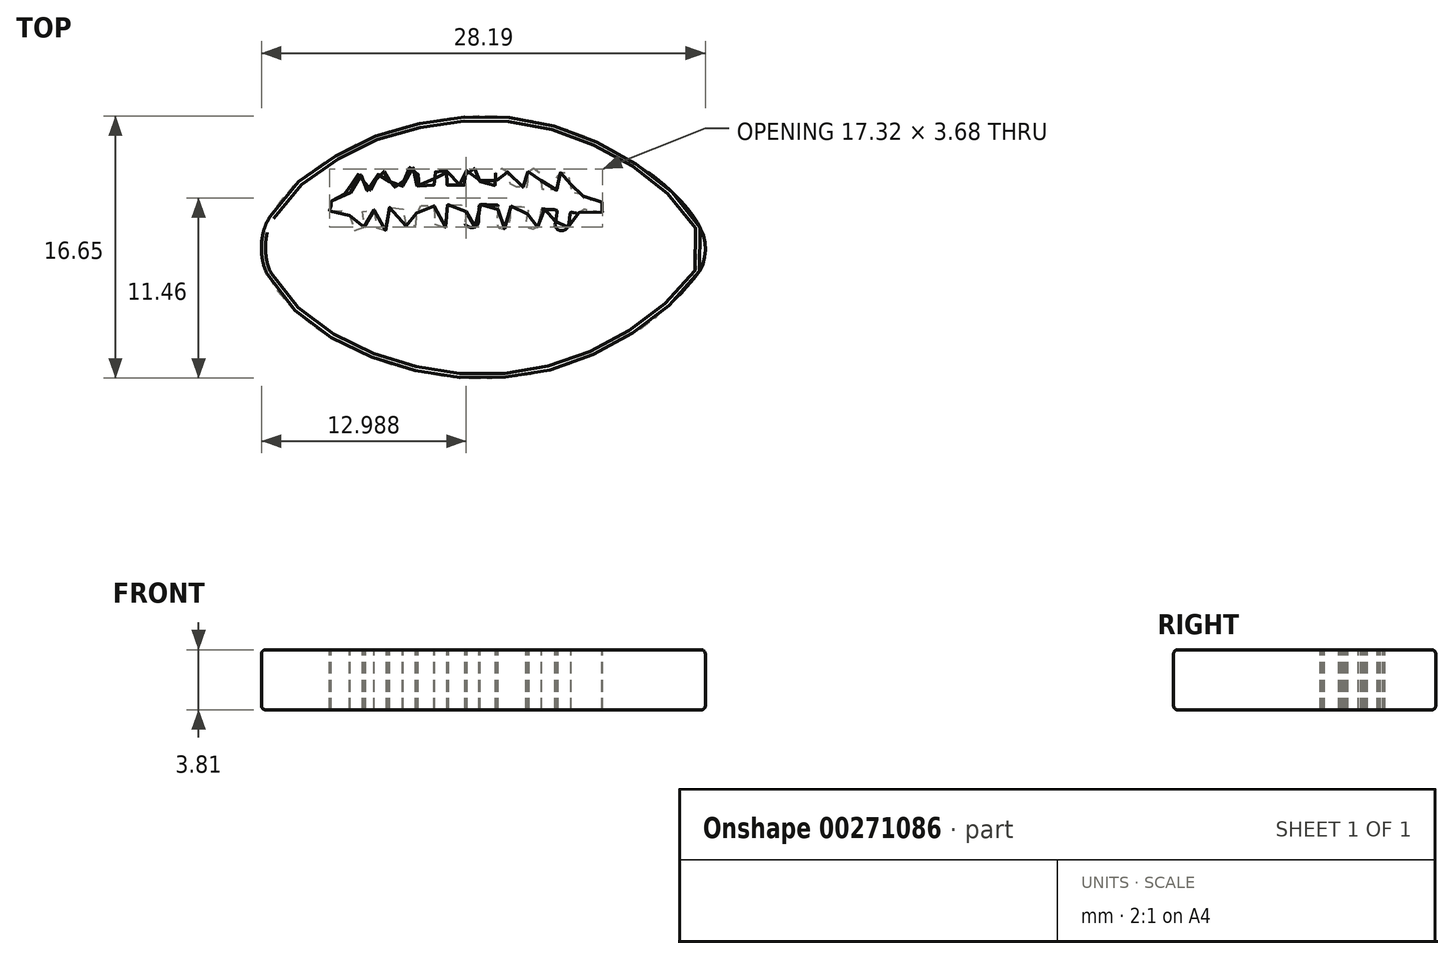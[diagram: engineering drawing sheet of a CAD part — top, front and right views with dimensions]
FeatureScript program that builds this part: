
annotation { "Feature Type Name" : "Feature", "Feature Type Description" : "" }
export const myFeature = defineFeature(function(context is Context, id is Id, definition is map)
    precondition{}
    {
        {
            var Q0;
            Q0=qCreatedBy(makeId("Top.planeOp"),FACE);
            var sketch = newSketch(context, id + "F0", { "sketchPlane" : qUnion([Q0])});
            skPoint(sketch, "E0.middle", {"position": v(0, 0) * mm});
            skFitSpline(sketch, "E1", {"points": [v(13.84, -7.05) * mm, v(13.82, -6.2) * mm, v(13.09, -4.68) * mm, v(11.7, -3.12) * mm, v(9.63, -1.48) * mm, v(6.3, 0.3) * mm, v(3.7, 1.17) * mm, v(0.26, 1.65) * mm, v(-2.3, 1.5) * mm, v(-4.49, 1.14) * mm, v(-6.86, 0.47) * mm, v(-9, -0.52) * mm, v(-11.7, -2.3) * mm, v(-13.11, -3.7) * mm, v(-13.78, -4.7) * mm, v(-14.2, -5.68) * mm, v(-14.3, -7.18) * mm, v(-13.94, -8.42) * mm, v(-12.7, -10.18) * mm, v(-11.83, -10.98) * mm, v(-10.38, -12.1) * mm, v(-9.15, -12.8) * mm, v(-7.28, -13.67) * mm, v(-4.61, -14.5) * mm, v(-1.94, -14.93) * mm, v(0.3, -14.98) * mm, v(3.1, -14.66) * mm, v(5.1, -14.13) * mm, v(6.84, -13.43) * mm, v(9.64, -11.88) * mm, v(11.3, -10.59) * mm, v(12.98, -8.86) * mm, v(13.7, -7.76) * mm, v(13.84, -7.05) * mm]});
            skArc(sketch, "E2", {"start": v(-11.9, -3.32) * mm, "mid": v(-12, -3.9) * mm, "end": v(-12.07, -4.47) * mm});
            skArc(sketch, "E3", {"start": v(-9.3, -1.43) * mm, "mid": v(-9.63, -2.58) * mm, "end": v(-9.87, -3.74) * mm});
            skArc(sketch, "E4", {"start": v(9.72, -11.06) * mm, "mid": v(9.89, -8.05) * mm, "end": v(9.87, -5.03) * mm});
            skArc(sketch, "E5", {"start": v(6.96, -12.67) * mm, "mid": v(7.34, -8.57) * mm, "end": v(7.33, -4.45) * mm});
            skArc(sketch, "E6", {"start": v(13.23, -6.62) * mm, "mid": v(11.6, -5.7) * mm, "end": v(9.87, -5.03) * mm});
            skArc(sketch, "E7", {"start": v(12.96, -5.7) * mm, "mid": v(11.43, -4.97) * mm, "end": v(9.85, -4.37) * mm});
            skArc(sketch, "E8", {"start": v(-12.13, -5.1) * mm, "mid": v(-12.95, -5.5) * mm, "end": v(-13.64, -6.09) * mm});
            skArc(sketch, "E9", {"start": v(-12.07, -4.47) * mm, "mid": v(-12.65, -4.7) * mm, "end": v(-13.2, -4.99) * mm});
            skFitSpline(sketch, "E10", {"points": [v(-9.97, -4.38) * mm, v(-9.32, -4.28) * mm, v(-9.2, -4.31) * mm, v(-9.03, -4.45) * mm, v(-8.74, -4.5) * mm, v(-8.71, -4.66) * mm, v(-8.6, -5.39) * mm, v(-8.29, -5.65) * mm, v(-7.97, -5.6) * mm, v(-7.81, -5.38) * mm, v(-7.79, -5.18) * mm, v(-7.89, -4.38) * mm, v(-7.78, -4.35) * mm, v(-7.2, -4.28) * mm, v(-7.17, -4.4) * mm, v(-7.05, -5.35) * mm, v(-6.93, -5.58) * mm, v(-6.62, -5.67) * mm, v(-6.35, -5.53) * mm, v(-6.23, -5.3) * mm, v(-6.24, -5.08) * mm, v(-6.36, -4.18) * mm, v(-6.23, -4.14) * mm, v(-5.37, -4.08) * mm, v(-5.35, -4.27) * mm, v(-5.23, -5.12) * mm, v(-5.06, -5.36) * mm, v(-4.74, -5.4) * mm, v(-4.52, -5.27) * mm, v(-4.4, -5.04) * mm, v(-4.43, -4.76) * mm, v(-4.53, -4.03) * mm, v(-4.4, -4.02) * mm, v(-3.8, -3.98) * mm, v(-3.4, -3.97) * mm, v(-3.36, -4.2) * mm, v(-3.32, -5.2) * mm, v(-3.11, -5.42) * mm, v(-2.74, -5.44) * mm, v(-2.52, -5.24) * mm, v(-2.5, -5.07) * mm, v(-2.51, -4.72) * mm, v(-2.53, -4.16) * mm, v(-2.5, -3.98) * mm, v(-2.2, -3.94) * mm, v(-1.66, -3.96) * mm, v(-1.32, -3.96) * mm, v(-1.32, -4.24) * mm, v(-1.36, -4.72) * mm, v(-1.41, -5.06) * mm, v(-1.3, -5.3) * mm, v(-0.98, -5.42) * mm, v(-0.7, -5.34) * mm, v(-0.57, -5.12) * mm, v(-0.53, -4.72) * mm, v(-0.48, -4.3) * mm, v(-0.46, -3.98) * mm, v(-0.17, -3.96) * mm, v(0.14, -3.98) * mm, v(0.48, -3.98) * mm, v(0.7, -4) * mm, v(0.7, -4.23) * mm, v(0.63, -4.86) * mm, v(0.6, -5.13) * mm, v(0.72, -5.4) * mm, v(0.97, -5.5) * mm, v(1.2, -5.46) * mm, v(1.37, -5.3) * mm, v(1.46, -4.91) * mm, v(1.5, -4.54) * mm, v(1.55, -4.05) * mm, v(1.7, -4.05) * mm, v(2.04, -4.1) * mm, v(2.63, -4.12) * mm, v(2.63, -4.26) * mm, v(2.52, -4.76) * mm, v(2.48, -5.16) * mm, v(2.64, -5.44) * mm, v(2.97, -5.5) * mm, v(3.22, -5.37) * mm, v(3.32, -5.08) * mm, v(3.38, -4.74) * mm, v(3.43, -4.48) * mm, v(3.45, -4.24) * mm, v(3.71, -4.25) * mm, v(4.06, -4.28) * mm, v(4.45, -4.34) * mm, v(4.45, -4.49) * mm, v(4.39, -4.86) * mm, v(4.33, -5.22) * mm, v(4.37, -5.4) * mm, v(4.55, -5.57) * mm, v(4.83, -5.6) * mm, v(5.05, -5.5) * mm, v(5.16, -5.33) * mm, v(5.21, -5.07) * mm, v(5.3, -4.45) * mm, v(5.38, -4.45) * mm, v(5.7, -4.49) * mm, v(5.95, -4.41) * mm, v(6.12, -4.27) * mm, v(6.37, -4.28) * mm, v(6.9, -4.38) * mm, v(7.33, -4.45) * mm, v(7.32, -4.4) * mm, v(7.31, -4.18) * mm, v(7.3, -3.84) * mm, v(7.29, -3.8) * mm, v(7, -3.76) * mm, v(6.52, -3.68) * mm, v(6.23, -3.65) * mm, v(6.16, -3.52) * mm, v(6.05, -3.37) * mm, v(5.83, -3.24) * mm, v(5.34, -3.19) * mm, v(5.33, -3.1) * mm, v(5.31, -2.75) * mm, v(5.26, -2.45) * mm, v(5.22, -2.22) * mm, v(5.1, -2.01) * mm, v(4.92, -1.94) * mm, v(4.7, -1.92) * mm, v(4.5, -2.05) * mm, v(4.37, -2.26) * mm, v(4.42, -2.57) * mm, v(4.5, -3.05) * mm, v(4.39, -3.04) * mm, v(3.97, -3) * mm, v(3.51, -2.98) * mm, v(3.48, -2.81) * mm, v(3.43, -2.4) * mm, v(3.35, -1.99) * mm, v(3.19, -1.78) * mm, v(2.93, -1.69) * mm, v(2.66, -1.8) * mm, v(2.54, -2.06) * mm, v(2.54, -2.33) * mm, v(2.65, -2.86) * mm, v(2.5, -2.88) * mm, v(2.08, -2.85) * mm, v(1.52, -2.82) * mm, v(1.5, -2.6) * mm, v(1.34, -1.93) * mm, v(1.15, -1.75) * mm, v(0.86, -1.68) * mm, v(0.6, -1.86) * mm, v(0.54, -2.2) * mm, v(0.67, -2.74) * mm, v(0.47, -2.74) * mm, v(-0.4, -2.7) * mm, v(-0.45, -2.53) * mm, v(-0.5, -1.96) * mm, v(-0.68, -1.72) * mm, v(-0.95, -1.63) * mm, v(-1.23, -1.72) * mm, v(-1.37, -1.97) * mm, v(-1.31, -2.26) * mm, v(-1.29, -2.7) * mm, v(-1.43, -2.72) * mm, v(-1.95, -2.7) * mm, v(-2.53, -2.72) * mm, v(-2.5, -2.54) * mm, v(-2.45, -2.03) * mm, v(-2.63, -1.75) * mm, v(-2.9, -1.66) * mm, v(-3.24, -1.8) * mm, v(-3.3, -2.07) * mm, v(-3.34, -2.43) * mm, v(-3.35, -2.7) * mm, v(-3.56, -2.7) * mm, v(-3.92, -2.72) * mm, v(-4.48, -2.75) * mm, v(-4.47, -2.57) * mm, v(-4.37, -2.1) * mm, v(-4.43, -1.8) * mm, v(-4.65, -1.63) * mm, v(-4.94, -1.6) * mm, v(-5.15, -1.8) * mm, v(-5.26, -2.17) * mm, v(-5.36, -2.8) * mm, v(-5.5, -2.85) * mm, v(-5.8, -2.85) * mm, v(-6.26, -2.9) * mm, v(-6.26, -2.75) * mm, v(-6.18, -2.36) * mm, v(-6.24, -2.09) * mm, v(-6.35, -1.93) * mm, v(-6.66, -1.86) * mm, v(-6.9, -2) * mm, v(-7, -2.23) * mm, v(-7.11, -2.57) * mm, v(-7.16, -2.98) * mm, v(-7.31, -3.02) * mm, v(-7.82, -3.1) * mm, v(-7.8, -2.9) * mm, v(-7.72, -2.54) * mm, v(-7.82, -2.23) * mm, v(-8.05, -2.06) * mm, v(-8.39, -2.12) * mm, v(-8.56, -2.37) * mm, v(-8.63, -2.7) * mm, v(-8.7, -3.25) * mm, v(-8.85, -3.25) * mm, v(-9.14, -3.37) * mm, v(-9.38, -3.66) * mm, v(-9.87, -3.74) * mm, v(-9.9, -3.87) * mm, v(-9.93, -4.14) * mm, v(-9.97, -4.38) * mm]});
            skFitSpline(sketch, "E11.0", {"points": [v(13.2, -7.07) * mm, v(13.21, -7) * mm, v(13.22, -6.92) * mm, v(13.22, -6.83) * mm, v(13.23, -6.71) * mm, v(13.23, -6.6) * mm, v(13.23, -6.53) * mm, v(13.22, -6.46) * mm, v(13.21, -6.41) * mm, v(13.2, -6.36) * mm, v(13.2, -6.3) * mm, v(13.16, -6.19) * mm, v(13.1, -6.02) * mm, v(13, -5.78) * mm, v(12.83, -5.45) * mm, v(12.57, -5.05) * mm, v(12.29, -4.66) * mm, v(11.97, -4.29) * mm, v(11.68, -3.98) * mm, v(11.43, -3.74) * mm, v(11.27, -3.59) * mm, v(11.14, -3.46) * mm, v(11, -3.35) * mm, v(10.77, -3.14) * mm, v(10.43, -2.84) * mm, v(9.97, -2.48) * mm, v(9.47, -2.13) * mm, v(8.91, -1.77) * mm, v(8.1, -1.29) * mm, v(7.24, -0.83) * mm, v(6.4, -0.43) * mm, v(5.61, -0.08) * mm, v(4.9, 0.18) * mm, v(4.18, 0.4) * mm, v(3.42, 0.58) * mm, v(2.54, 0.76) * mm, v(1.63, 0.9) * mm, v(1.07, 0.96) * mm, v(0.68, 1) * mm, v(0.47, 1) * mm, v(0.26, 1.02) * mm, v(0, 1.03) * mm, v(-0.3, 1.03) * mm, v(-0.6, 1.02) * mm, v(-0.97, 1) * mm, v(-1.43, 0.97) * mm, v(-1.98, 0.9) * mm, v(-2.52, 0.84) * mm, v(-3.04, 0.76) * mm, v(-3.48, 0.7) * mm, v(-3.83, 0.63) * mm, v(-4.18, 0.56) * mm, v(-4.63, 0.46) * mm, v(-5.18, 0.33) * mm, v(-5.73, 0.17) * mm, v(-6.27, 0) * mm, v(-6.78, -0.18) * mm, v(-7.26, -0.37) * mm, v(-7.74, -0.58) * mm, v(-8.14, -0.78) * mm, v(-8.48, -0.96) * mm, v(-8.74, -1.1) * mm, v(-9.01, -1.26) * mm, v(-9.38, -1.48) * mm, v(-9.86, -1.77) * mm, v(-10.33, -2.08) * mm, v(-10.68, -2.32) * mm, v(-10.94, -2.51) * mm, v(-11.18, -2.7) * mm, v(-11.41, -2.88) * mm, v(-11.62, -3.06) * mm, v(-11.88, -3.3) * mm, v(-12.17, -3.58) * mm, v(-12.46, -3.9) * mm, v(-12.67, -4.18) * mm, v(-12.82, -4.38) * mm, v(-12.97, -4.6) * mm, v(-13.08, -4.77) * mm, v(-13.16, -4.92) * mm, v(-13.2, -4.97) * mm, v(-13.23, -5.02) * mm, v(-13.26, -5.08) * mm, v(-13.3, -5.16) * mm, v(-13.35, -5.23) * mm, v(-13.4, -5.33) * mm, v(-13.44, -5.42) * mm, v(-13.48, -5.51) * mm, v(-13.5, -5.58) * mm, v(-13.54, -5.65) * mm, v(-13.56, -5.72) * mm, v(-13.57, -5.76) * mm, v(-13.58, -5.8) * mm, v(-13.6, -5.84) * mm, v(-13.6, -5.9) * mm, v(-13.62, -5.96) * mm, v(-13.63, -6.05) * mm, v(-13.65, -6.15) * mm, v(-13.66, -6.28) * mm, v(-13.68, -6.45) * mm, v(-13.68, -6.66) * mm, v(-13.68, -6.86) * mm, v(-13.67, -7.03) * mm, v(-13.66, -7.16) * mm, v(-13.65, -7.28) * mm, v(-13.64, -7.38) * mm, v(-13.62, -7.49) * mm, v(-13.6, -7.56) * mm, v(-13.58, -7.64) * mm, v(-13.56, -7.71) * mm, v(-13.53, -7.79) * mm, v(-13.5, -7.87) * mm, v(-13.47, -7.94) * mm, v(-13.4, -8.07) * mm, v(-13.34, -8.2) * mm, v(-13.27, -8.32) * mm, v(-13.2, -8.43) * mm, v(-13.14, -8.54) * mm, v(-13.04, -8.69) * mm, v(-12.95, -8.83) * mm, v(-12.84, -8.98) * mm, v(-12.76, -9.1) * mm, v(-12.68, -9.2) * mm, v(-12.6, -9.3) * mm, v(-12.52, -9.4) * mm, v(-12.44, -9.5) * mm, v(-12.37, -9.6) * mm, v(-12.3, -9.68) * mm, v(-12.22, -9.77) * mm, v(-12.15, -9.84) * mm, v(-12.09, -9.9) * mm, v(-12, -10) * mm, v(-11.92, -10.07) * mm, v(-11.84, -10.15) * mm, v(-11.77, -10.2) * mm, v(-11.7, -10.26) * mm, v(-11.61, -10.34) * mm, v(-11.49, -10.44) * mm, v(-11.25, -10.63) * mm, v(-10.94, -10.89) * mm, v(-10.54, -11.2) * mm, v(-10.24, -11.42) * mm, v(-10.06, -11.55) * mm, v(-9.93, -11.63) * mm, v(-9.79, -11.72) * mm, v(-9.62, -11.83) * mm, v(-9.44, -11.92) * mm, v(-9.3, -12) * mm, v(-9.18, -12.07) * mm, v(-9.05, -12.13) * mm, v(-8.88, -12.21) * mm, v(-8.6, -12.36) * mm, v(-8.24, -12.54) * mm, v(-7.77, -12.77) * mm, v(-7.36, -12.95) * mm, v(-7.05, -13.08) * mm, v(-6.88, -13.15) * mm, v(-6.61, -13.25) * mm, v(-6.02, -13.46) * mm, v(-5.05, -13.75) * mm, v(-4.05, -13.98) * mm, v(-3.26, -14.12) * mm, v(-2.77, -14.2) * mm, v(-2.4, -14.24) * mm, v(-2.02, -14.28) * mm, v(-1.57, -14.32) * mm, v(-1.05, -14.35) * mm, v(-0.53, -14.37) * mm, v(0, -14.36) * mm, v(0.57, -14.33) * mm, v(1.17, -14.29) * mm, v(1.79, -14.22) * mm, v(2.4, -14.14) * mm, v(3.17, -14) * mm, v(3.86, -13.84) * mm, v(4.5, -13.66) * mm, v(4.87, -13.54) * mm, v(5.16, -13.44) * mm, v(5.44, -13.34) * mm, v(5.8, -13.2) * mm, v(6.25, -13) * mm, v(6.76, -12.77) * mm, v(7.33, -12.48) * mm, v(7.83, -12.22) * mm, v(8.22, -12) * mm, v(8.62, -11.77) * mm, v(8.98, -11.55) * mm, v(9.32, -11.34) * mm, v(9.55, -11.18) * mm, v(9.76, -11.03) * mm, v(10.03, -10.84) * mm, v(10.28, -10.64) * mm, v(10.53, -10.43) * mm, v(10.72, -10.26) * mm, v(10.9, -10.08) * mm, v(11.18, -9.83) * mm, v(11.52, -9.5) * mm, v(11.93, -9.08) * mm, v(12.24, -8.74) * mm, v(12.47, -8.48) * mm, v(12.62, -8.3) * mm, v(12.76, -8.12) * mm, v(12.85, -8) * mm, v(12.92, -7.9) * mm, v(12.98, -7.8) * mm, v(13.03, -7.7) * mm, v(13.07, -7.63) * mm, v(13.1, -7.58) * mm, v(13.1, -7.55) * mm, v(13.12, -7.51) * mm, v(13.13, -7.47) * mm, v(13.15, -7.42) * mm, v(13.16, -7.37) * mm, v(13.17, -7.32) * mm, v(13.18, -7.24) * mm, v(13.2, -7.16) * mm, v(13.2, -7.07) * mm, v(13.21, -7) * mm, v(13.22, -6.92) * mm]});
            skArc(sketch, "E12.trimOffspring", {"start": v(-12.13, -5.1) * mm, "mid": v(-12.2, -7.55) * mm, "end": v(-12, -10) * mm});
            skArc(sketch, "E13.trimOffspring", {"start": v(-9.97, -4.38) * mm, "mid": v(-10.1, -8.19) * mm, "end": v(-9.42, -11.93) * mm});
            skFitSpline(sketch, "E14.trimOffspring", {"points": [v(13.2, -7.07) * mm, v(13.21, -7) * mm, v(13.22, -6.92) * mm, v(13.22, -6.83) * mm, v(13.23, -6.71) * mm, v(13.23, -6.6) * mm, v(13.23, -6.53) * mm, v(13.22, -6.46) * mm, v(13.21, -6.41) * mm, v(13.2, -6.36) * mm, v(13.2, -6.3) * mm, v(13.16, -6.19) * mm, v(13.1, -6.02) * mm, v(13, -5.78) * mm, v(12.83, -5.45) * mm, v(12.57, -5.05) * mm, v(12.29, -4.66) * mm, v(11.97, -4.29) * mm, v(11.68, -3.98) * mm, v(11.43, -3.74) * mm, v(11.27, -3.59) * mm, v(11.14, -3.46) * mm, v(11, -3.35) * mm, v(10.77, -3.14) * mm, v(10.43, -2.84) * mm, v(9.97, -2.48) * mm, v(9.47, -2.13) * mm, v(8.91, -1.77) * mm, v(8.1, -1.29) * mm, v(7.24, -0.83) * mm, v(6.4, -0.43) * mm, v(5.61, -0.08) * mm, v(4.9, 0.18) * mm, v(4.18, 0.4) * mm, v(3.42, 0.58) * mm, v(2.54, 0.76) * mm, v(1.63, 0.9) * mm, v(1.07, 0.96) * mm, v(0.68, 1) * mm, v(0.47, 1) * mm, v(0.26, 1.02) * mm, v(0, 1.03) * mm, v(-0.3, 1.03) * mm, v(-0.6, 1.02) * mm, v(-0.97, 1) * mm, v(-1.43, 0.97) * mm, v(-1.98, 0.9) * mm, v(-2.52, 0.84) * mm, v(-3.04, 0.76) * mm, v(-3.48, 0.7) * mm, v(-3.83, 0.63) * mm, v(-4.18, 0.56) * mm, v(-4.63, 0.46) * mm, v(-5.18, 0.33) * mm, v(-5.73, 0.17) * mm, v(-6.27, 0) * mm, v(-6.78, -0.18) * mm, v(-7.26, -0.37) * mm, v(-7.74, -0.58) * mm, v(-8.14, -0.78) * mm, v(-8.48, -0.96) * mm, v(-8.74, -1.1) * mm, v(-9.01, -1.26) * mm, v(-9.38, -1.48) * mm, v(-9.86, -1.77) * mm, v(-10.33, -2.08) * mm, v(-10.68, -2.32) * mm, v(-10.94, -2.51) * mm, v(-11.18, -2.7) * mm, v(-11.41, -2.88) * mm, v(-11.62, -3.06) * mm, v(-11.88, -3.3) * mm, v(-12.17, -3.58) * mm, v(-12.46, -3.9) * mm, v(-12.67, -4.18) * mm, v(-12.82, -4.38) * mm, v(-12.97, -4.6) * mm, v(-13.08, -4.77) * mm, v(-13.16, -4.92) * mm, v(-13.2, -4.97) * mm, v(-13.23, -5.02) * mm, v(-13.26, -5.08) * mm, v(-13.3, -5.16) * mm, v(-13.35, -5.23) * mm, v(-13.4, -5.33) * mm, v(-13.44, -5.42) * mm, v(-13.48, -5.51) * mm, v(-13.5, -5.58) * mm, v(-13.54, -5.65) * mm, v(-13.56, -5.72) * mm, v(-13.57, -5.76) * mm, v(-13.58, -5.8) * mm, v(-13.6, -5.84) * mm, v(-13.6, -5.9) * mm, v(-13.62, -5.96) * mm, v(-13.63, -6.05) * mm, v(-13.65, -6.15) * mm, v(-13.66, -6.28) * mm, v(-13.68, -6.45) * mm, v(-13.68, -6.66) * mm, v(-13.68, -6.86) * mm, v(-13.67, -7.03) * mm, v(-13.66, -7.16) * mm, v(-13.65, -7.28) * mm, v(-13.64, -7.38) * mm, v(-13.62, -7.49) * mm, v(-13.6, -7.56) * mm, v(-13.58, -7.64) * mm, v(-13.56, -7.71) * mm, v(-13.53, -7.79) * mm, v(-13.5, -7.87) * mm, v(-13.47, -7.94) * mm, v(-13.4, -8.07) * mm, v(-13.34, -8.2) * mm, v(-13.27, -8.32) * mm, v(-13.2, -8.43) * mm, v(-13.14, -8.54) * mm, v(-13.04, -8.69) * mm, v(-12.95, -8.83) * mm, v(-12.84, -8.98) * mm, v(-12.76, -9.1) * mm, v(-12.68, -9.2) * mm, v(-12.6, -9.3) * mm, v(-12.52, -9.4) * mm, v(-12.44, -9.5) * mm, v(-12.37, -9.6) * mm, v(-12.3, -9.68) * mm, v(-12.22, -9.77) * mm, v(-12.15, -9.84) * mm, v(-12.09, -9.9) * mm, v(-12, -10) * mm, v(-11.92, -10.07) * mm, v(-11.84, -10.15) * mm, v(-11.77, -10.2) * mm, v(-11.7, -10.26) * mm, v(-11.61, -10.34) * mm, v(-11.49, -10.44) * mm, v(-11.25, -10.63) * mm, v(-10.94, -10.89) * mm, v(-10.54, -11.2) * mm, v(-10.24, -11.42) * mm, v(-10.06, -11.55) * mm, v(-9.93, -11.63) * mm, v(-9.79, -11.72) * mm, v(-9.62, -11.83) * mm, v(-9.44, -11.92) * mm, v(-9.3, -12) * mm, v(-9.18, -12.07) * mm, v(-9.05, -12.13) * mm, v(-8.88, -12.21) * mm, v(-8.6, -12.36) * mm, v(-8.24, -12.54) * mm, v(-7.77, -12.77) * mm, v(-7.36, -12.95) * mm, v(-7.05, -13.08) * mm, v(-6.88, -13.15) * mm, v(-6.61, -13.25) * mm, v(-6.02, -13.46) * mm, v(-5.05, -13.75) * mm, v(-4.05, -13.98) * mm, v(-3.26, -14.12) * mm, v(-2.77, -14.2) * mm, v(-2.4, -14.24) * mm, v(-2.02, -14.28) * mm, v(-1.57, -14.32) * mm, v(-1.05, -14.35) * mm, v(-0.53, -14.37) * mm, v(0, -14.36) * mm, v(0.57, -14.33) * mm, v(1.17, -14.29) * mm, v(1.79, -14.22) * mm, v(2.4, -14.14) * mm, v(3.17, -14) * mm, v(3.86, -13.84) * mm, v(4.5, -13.66) * mm, v(4.87, -13.54) * mm, v(5.16, -13.44) * mm, v(5.44, -13.34) * mm, v(5.8, -13.2) * mm, v(6.25, -13) * mm, v(6.76, -12.77) * mm, v(7.33, -12.48) * mm, v(7.83, -12.22) * mm, v(8.22, -12) * mm, v(8.62, -11.77) * mm, v(8.98, -11.55) * mm, v(9.32, -11.34) * mm, v(9.55, -11.18) * mm, v(9.76, -11.03) * mm, v(10.03, -10.84) * mm, v(10.28, -10.64) * mm, v(10.53, -10.43) * mm, v(10.72, -10.26) * mm, v(10.9, -10.08) * mm, v(11.18, -9.83) * mm, v(11.52, -9.5) * mm, v(11.93, -9.08) * mm, v(12.24, -8.74) * mm, v(12.47, -8.48) * mm, v(12.62, -8.3) * mm, v(12.76, -8.12) * mm, v(12.85, -8) * mm, v(12.92, -7.9) * mm, v(12.98, -7.8) * mm, v(13.03, -7.7) * mm, v(13.07, -7.63) * mm, v(13.1, -7.58) * mm, v(13.1, -7.55) * mm, v(13.12, -7.51) * mm, v(13.13, -7.47) * mm, v(13.15, -7.42) * mm, v(13.16, -7.37) * mm, v(13.17, -7.32) * mm, v(13.18, -7.24) * mm, v(13.2, -7.16) * mm, v(13.2, -7.07) * mm, v(13.21, -7) * mm, v(13.22, -6.92) * mm]});
            skFitSpline(sketch, "E15.trimOffspring", {"points": [v(13.2, -7.07) * mm, v(13.21, -7) * mm, v(13.22, -6.92) * mm, v(13.22, -6.83) * mm, v(13.23, -6.71) * mm, v(13.23, -6.6) * mm, v(13.23, -6.53) * mm, v(13.22, -6.46) * mm, v(13.21, -6.41) * mm, v(13.2, -6.36) * mm, v(13.2, -6.3) * mm, v(13.16, -6.19) * mm, v(13.1, -6.02) * mm, v(13, -5.78) * mm, v(12.83, -5.45) * mm, v(12.57, -5.05) * mm, v(12.29, -4.66) * mm, v(11.97, -4.29) * mm, v(11.68, -3.98) * mm, v(11.43, -3.74) * mm, v(11.27, -3.59) * mm, v(11.14, -3.46) * mm, v(11, -3.35) * mm, v(10.77, -3.14) * mm, v(10.43, -2.84) * mm, v(9.97, -2.48) * mm, v(9.47, -2.13) * mm, v(8.91, -1.77) * mm, v(8.1, -1.29) * mm, v(7.24, -0.83) * mm, v(6.4, -0.43) * mm, v(5.61, -0.08) * mm, v(4.9, 0.18) * mm, v(4.18, 0.4) * mm, v(3.42, 0.58) * mm, v(2.54, 0.76) * mm, v(1.63, 0.9) * mm, v(1.07, 0.96) * mm, v(0.68, 1) * mm, v(0.47, 1) * mm, v(0.26, 1.02) * mm, v(0, 1.03) * mm, v(-0.3, 1.03) * mm, v(-0.6, 1.02) * mm, v(-0.97, 1) * mm, v(-1.43, 0.97) * mm, v(-1.98, 0.9) * mm, v(-2.52, 0.84) * mm, v(-3.04, 0.76) * mm, v(-3.48, 0.7) * mm, v(-3.83, 0.63) * mm, v(-4.18, 0.56) * mm, v(-4.63, 0.46) * mm, v(-5.18, 0.33) * mm, v(-5.73, 0.17) * mm, v(-6.27, 0) * mm, v(-6.78, -0.18) * mm, v(-7.26, -0.37) * mm, v(-7.74, -0.58) * mm, v(-8.14, -0.78) * mm, v(-8.48, -0.96) * mm, v(-8.74, -1.1) * mm, v(-9.01, -1.26) * mm, v(-9.38, -1.48) * mm, v(-9.86, -1.77) * mm, v(-10.33, -2.08) * mm, v(-10.68, -2.32) * mm, v(-10.94, -2.51) * mm, v(-11.18, -2.7) * mm, v(-11.41, -2.88) * mm, v(-11.62, -3.06) * mm, v(-11.88, -3.3) * mm, v(-12.17, -3.58) * mm, v(-12.46, -3.9) * mm, v(-12.67, -4.18) * mm, v(-12.82, -4.38) * mm, v(-12.97, -4.6) * mm, v(-13.08, -4.77) * mm, v(-13.16, -4.92) * mm, v(-13.2, -4.97) * mm, v(-13.23, -5.02) * mm, v(-13.26, -5.08) * mm, v(-13.3, -5.16) * mm, v(-13.35, -5.23) * mm, v(-13.4, -5.33) * mm, v(-13.44, -5.42) * mm, v(-13.48, -5.51) * mm, v(-13.5, -5.58) * mm, v(-13.54, -5.65) * mm, v(-13.56, -5.72) * mm, v(-13.57, -5.76) * mm, v(-13.58, -5.8) * mm, v(-13.6, -5.84) * mm, v(-13.6, -5.9) * mm, v(-13.62, -5.96) * mm, v(-13.63, -6.05) * mm, v(-13.65, -6.15) * mm, v(-13.66, -6.28) * mm, v(-13.68, -6.45) * mm, v(-13.68, -6.66) * mm, v(-13.68, -6.86) * mm, v(-13.67, -7.03) * mm, v(-13.66, -7.16) * mm, v(-13.65, -7.28) * mm, v(-13.64, -7.38) * mm, v(-13.62, -7.49) * mm, v(-13.6, -7.56) * mm, v(-13.58, -7.64) * mm, v(-13.56, -7.71) * mm, v(-13.53, -7.79) * mm, v(-13.5, -7.87) * mm, v(-13.47, -7.94) * mm, v(-13.4, -8.07) * mm, v(-13.34, -8.2) * mm, v(-13.27, -8.32) * mm, v(-13.2, -8.43) * mm, v(-13.14, -8.54) * mm, v(-13.04, -8.69) * mm, v(-12.95, -8.83) * mm, v(-12.84, -8.98) * mm, v(-12.76, -9.1) * mm, v(-12.68, -9.2) * mm, v(-12.6, -9.3) * mm, v(-12.52, -9.4) * mm, v(-12.44, -9.5) * mm, v(-12.37, -9.6) * mm, v(-12.3, -9.68) * mm, v(-12.22, -9.77) * mm, v(-12.15, -9.84) * mm, v(-12.09, -9.9) * mm, v(-12, -10) * mm, v(-11.92, -10.07) * mm, v(-11.84, -10.15) * mm, v(-11.77, -10.2) * mm, v(-11.7, -10.26) * mm, v(-11.61, -10.34) * mm, v(-11.49, -10.44) * mm, v(-11.25, -10.63) * mm, v(-10.94, -10.89) * mm, v(-10.54, -11.2) * mm, v(-10.24, -11.42) * mm, v(-10.06, -11.55) * mm, v(-9.93, -11.63) * mm, v(-9.79, -11.72) * mm, v(-9.62, -11.83) * mm, v(-9.44, -11.92) * mm, v(-9.3, -12) * mm, v(-9.18, -12.07) * mm, v(-9.05, -12.13) * mm, v(-8.88, -12.21) * mm, v(-8.6, -12.36) * mm, v(-8.24, -12.54) * mm, v(-7.77, -12.77) * mm, v(-7.36, -12.95) * mm, v(-7.05, -13.08) * mm, v(-6.88, -13.15) * mm, v(-6.61, -13.25) * mm, v(-6.02, -13.46) * mm, v(-5.05, -13.75) * mm, v(-4.05, -13.98) * mm, v(-3.26, -14.12) * mm, v(-2.77, -14.2) * mm, v(-2.4, -14.24) * mm, v(-2.02, -14.28) * mm, v(-1.57, -14.32) * mm, v(-1.05, -14.35) * mm, v(-0.53, -14.37) * mm, v(0, -14.36) * mm, v(0.57, -14.33) * mm, v(1.17, -14.29) * mm, v(1.79, -14.22) * mm, v(2.4, -14.14) * mm, v(3.17, -14) * mm, v(3.86, -13.84) * mm, v(4.5, -13.66) * mm, v(4.87, -13.54) * mm, v(5.16, -13.44) * mm, v(5.44, -13.34) * mm, v(5.8, -13.2) * mm, v(6.25, -13) * mm, v(6.76, -12.77) * mm, v(7.33, -12.48) * mm, v(7.83, -12.22) * mm, v(8.22, -12) * mm, v(8.62, -11.77) * mm, v(8.98, -11.55) * mm, v(9.32, -11.34) * mm, v(9.55, -11.18) * mm, v(9.76, -11.03) * mm, v(10.03, -10.84) * mm, v(10.28, -10.64) * mm, v(10.53, -10.43) * mm, v(10.72, -10.26) * mm, v(10.9, -10.08) * mm, v(11.18, -9.83) * mm, v(11.52, -9.5) * mm, v(11.93, -9.08) * mm, v(12.24, -8.74) * mm, v(12.47, -8.48) * mm, v(12.62, -8.3) * mm, v(12.76, -8.12) * mm, v(12.85, -8) * mm, v(12.92, -7.9) * mm, v(12.98, -7.8) * mm, v(13.03, -7.7) * mm, v(13.07, -7.63) * mm, v(13.1, -7.58) * mm, v(13.1, -7.55) * mm, v(13.12, -7.51) * mm, v(13.13, -7.47) * mm, v(13.15, -7.42) * mm, v(13.16, -7.37) * mm, v(13.17, -7.32) * mm, v(13.18, -7.24) * mm, v(13.2, -7.16) * mm, v(13.2, -7.07) * mm, v(13.21, -7) * mm, v(13.22, -6.92) * mm]});
            skFitSpline(sketch, "E16.trimOffspring", {"points": [v(13.2, -7.07) * mm, v(13.21, -7) * mm, v(13.22, -6.92) * mm, v(13.22, -6.83) * mm, v(13.23, -6.71) * mm, v(13.23, -6.6) * mm, v(13.23, -6.53) * mm, v(13.22, -6.46) * mm, v(13.21, -6.41) * mm, v(13.2, -6.36) * mm, v(13.2, -6.3) * mm, v(13.16, -6.19) * mm, v(13.1, -6.02) * mm, v(13, -5.78) * mm, v(12.83, -5.45) * mm, v(12.57, -5.05) * mm, v(12.29, -4.66) * mm, v(11.97, -4.29) * mm, v(11.68, -3.98) * mm, v(11.43, -3.74) * mm, v(11.27, -3.59) * mm, v(11.14, -3.46) * mm, v(11, -3.35) * mm, v(10.77, -3.14) * mm, v(10.43, -2.84) * mm, v(9.97, -2.48) * mm, v(9.47, -2.13) * mm, v(8.91, -1.77) * mm, v(8.1, -1.29) * mm, v(7.24, -0.83) * mm, v(6.4, -0.43) * mm, v(5.61, -0.08) * mm, v(4.9, 0.18) * mm, v(4.18, 0.4) * mm, v(3.42, 0.58) * mm, v(2.54, 0.76) * mm, v(1.63, 0.9) * mm, v(1.07, 0.96) * mm, v(0.68, 1) * mm, v(0.47, 1) * mm, v(0.26, 1.02) * mm, v(0, 1.03) * mm, v(-0.3, 1.03) * mm, v(-0.6, 1.02) * mm, v(-0.97, 1) * mm, v(-1.43, 0.97) * mm, v(-1.98, 0.9) * mm, v(-2.52, 0.84) * mm, v(-3.04, 0.76) * mm, v(-3.48, 0.7) * mm, v(-3.83, 0.63) * mm, v(-4.18, 0.56) * mm, v(-4.63, 0.46) * mm, v(-5.18, 0.33) * mm, v(-5.73, 0.17) * mm, v(-6.27, 0) * mm, v(-6.78, -0.18) * mm, v(-7.26, -0.37) * mm, v(-7.74, -0.58) * mm, v(-8.14, -0.78) * mm, v(-8.48, -0.96) * mm, v(-8.74, -1.1) * mm, v(-9.01, -1.26) * mm, v(-9.38, -1.48) * mm, v(-9.86, -1.77) * mm, v(-10.33, -2.08) * mm, v(-10.68, -2.32) * mm, v(-10.94, -2.51) * mm, v(-11.18, -2.7) * mm, v(-11.41, -2.88) * mm, v(-11.62, -3.06) * mm, v(-11.88, -3.3) * mm, v(-12.17, -3.58) * mm, v(-12.46, -3.9) * mm, v(-12.67, -4.18) * mm, v(-12.82, -4.38) * mm, v(-12.97, -4.6) * mm, v(-13.08, -4.77) * mm, v(-13.16, -4.92) * mm, v(-13.2, -4.97) * mm, v(-13.23, -5.02) * mm, v(-13.26, -5.08) * mm, v(-13.3, -5.16) * mm, v(-13.35, -5.23) * mm, v(-13.4, -5.33) * mm, v(-13.44, -5.42) * mm, v(-13.48, -5.51) * mm, v(-13.5, -5.58) * mm, v(-13.54, -5.65) * mm, v(-13.56, -5.72) * mm, v(-13.57, -5.76) * mm, v(-13.58, -5.8) * mm, v(-13.6, -5.84) * mm, v(-13.6, -5.9) * mm, v(-13.62, -5.96) * mm, v(-13.63, -6.05) * mm, v(-13.65, -6.15) * mm, v(-13.66, -6.28) * mm, v(-13.68, -6.45) * mm, v(-13.68, -6.66) * mm, v(-13.68, -6.86) * mm, v(-13.67, -7.03) * mm, v(-13.66, -7.16) * mm, v(-13.65, -7.28) * mm, v(-13.64, -7.38) * mm, v(-13.62, -7.49) * mm, v(-13.6, -7.56) * mm, v(-13.58, -7.64) * mm, v(-13.56, -7.71) * mm, v(-13.53, -7.79) * mm, v(-13.5, -7.87) * mm, v(-13.47, -7.94) * mm, v(-13.4, -8.07) * mm, v(-13.34, -8.2) * mm, v(-13.27, -8.32) * mm, v(-13.2, -8.43) * mm, v(-13.14, -8.54) * mm, v(-13.04, -8.69) * mm, v(-12.95, -8.83) * mm, v(-12.84, -8.98) * mm, v(-12.76, -9.1) * mm, v(-12.68, -9.2) * mm, v(-12.6, -9.3) * mm, v(-12.52, -9.4) * mm, v(-12.44, -9.5) * mm, v(-12.37, -9.6) * mm, v(-12.3, -9.68) * mm, v(-12.22, -9.77) * mm, v(-12.15, -9.84) * mm, v(-12.09, -9.9) * mm, v(-12, -10) * mm, v(-11.92, -10.07) * mm, v(-11.84, -10.15) * mm, v(-11.77, -10.2) * mm, v(-11.7, -10.26) * mm, v(-11.61, -10.34) * mm, v(-11.49, -10.44) * mm, v(-11.25, -10.63) * mm, v(-10.94, -10.89) * mm, v(-10.54, -11.2) * mm, v(-10.24, -11.42) * mm, v(-10.06, -11.55) * mm, v(-9.93, -11.63) * mm, v(-9.79, -11.72) * mm, v(-9.62, -11.83) * mm, v(-9.44, -11.92) * mm, v(-9.3, -12) * mm, v(-9.18, -12.07) * mm, v(-9.05, -12.13) * mm, v(-8.88, -12.21) * mm, v(-8.6, -12.36) * mm, v(-8.24, -12.54) * mm, v(-7.77, -12.77) * mm, v(-7.36, -12.95) * mm, v(-7.05, -13.08) * mm, v(-6.88, -13.15) * mm, v(-6.61, -13.25) * mm, v(-6.02, -13.46) * mm, v(-5.05, -13.75) * mm, v(-4.05, -13.98) * mm, v(-3.26, -14.12) * mm, v(-2.77, -14.2) * mm, v(-2.4, -14.24) * mm, v(-2.02, -14.28) * mm, v(-1.57, -14.32) * mm, v(-1.05, -14.35) * mm, v(-0.53, -14.37) * mm, v(0, -14.36) * mm, v(0.57, -14.33) * mm, v(1.17, -14.29) * mm, v(1.79, -14.22) * mm, v(2.4, -14.14) * mm, v(3.17, -14) * mm, v(3.86, -13.84) * mm, v(4.5, -13.66) * mm, v(4.87, -13.54) * mm, v(5.16, -13.44) * mm, v(5.44, -13.34) * mm, v(5.8, -13.2) * mm, v(6.25, -13) * mm, v(6.76, -12.77) * mm, v(7.33, -12.48) * mm, v(7.83, -12.22) * mm, v(8.22, -12) * mm, v(8.62, -11.77) * mm, v(8.98, -11.55) * mm, v(9.32, -11.34) * mm, v(9.55, -11.18) * mm, v(9.76, -11.03) * mm, v(10.03, -10.84) * mm, v(10.28, -10.64) * mm, v(10.53, -10.43) * mm, v(10.72, -10.26) * mm, v(10.9, -10.08) * mm, v(11.18, -9.83) * mm, v(11.52, -9.5) * mm, v(11.93, -9.08) * mm, v(12.24, -8.74) * mm, v(12.47, -8.48) * mm, v(12.62, -8.3) * mm, v(12.76, -8.12) * mm, v(12.85, -8) * mm, v(12.92, -7.9) * mm, v(12.98, -7.8) * mm, v(13.03, -7.7) * mm, v(13.07, -7.63) * mm, v(13.1, -7.58) * mm, v(13.1, -7.55) * mm, v(13.12, -7.51) * mm, v(13.13, -7.47) * mm, v(13.15, -7.42) * mm, v(13.16, -7.37) * mm, v(13.17, -7.32) * mm, v(13.18, -7.24) * mm, v(13.2, -7.16) * mm, v(13.2, -7.07) * mm, v(13.21, -7) * mm, v(13.22, -6.92) * mm]});
            skFitSpline(sketch, "E17.trimOffspring", {"points": [v(13.2, -7.07) * mm, v(13.21, -7) * mm, v(13.22, -6.92) * mm, v(13.22, -6.83) * mm, v(13.23, -6.71) * mm, v(13.23, -6.6) * mm, v(13.23, -6.53) * mm, v(13.22, -6.46) * mm, v(13.21, -6.41) * mm, v(13.2, -6.36) * mm, v(13.2, -6.3) * mm, v(13.16, -6.19) * mm, v(13.1, -6.02) * mm, v(13, -5.78) * mm, v(12.83, -5.45) * mm, v(12.57, -5.05) * mm, v(12.29, -4.66) * mm, v(11.97, -4.29) * mm, v(11.68, -3.98) * mm, v(11.43, -3.74) * mm, v(11.27, -3.59) * mm, v(11.14, -3.46) * mm, v(11, -3.35) * mm, v(10.77, -3.14) * mm, v(10.43, -2.84) * mm, v(9.97, -2.48) * mm, v(9.47, -2.13) * mm, v(8.91, -1.77) * mm, v(8.1, -1.29) * mm, v(7.24, -0.83) * mm, v(6.4, -0.43) * mm, v(5.61, -0.08) * mm, v(4.9, 0.18) * mm, v(4.18, 0.4) * mm, v(3.42, 0.58) * mm, v(2.54, 0.76) * mm, v(1.63, 0.9) * mm, v(1.07, 0.96) * mm, v(0.68, 1) * mm, v(0.47, 1) * mm, v(0.26, 1.02) * mm, v(0, 1.03) * mm, v(-0.3, 1.03) * mm, v(-0.6, 1.02) * mm, v(-0.97, 1) * mm, v(-1.43, 0.97) * mm, v(-1.98, 0.9) * mm, v(-2.52, 0.84) * mm, v(-3.04, 0.76) * mm, v(-3.48, 0.7) * mm, v(-3.83, 0.63) * mm, v(-4.18, 0.56) * mm, v(-4.63, 0.46) * mm, v(-5.18, 0.33) * mm, v(-5.73, 0.17) * mm, v(-6.27, 0) * mm, v(-6.78, -0.18) * mm, v(-7.26, -0.37) * mm, v(-7.74, -0.58) * mm, v(-8.14, -0.78) * mm, v(-8.48, -0.96) * mm, v(-8.74, -1.1) * mm, v(-9.01, -1.26) * mm, v(-9.38, -1.48) * mm, v(-9.86, -1.77) * mm, v(-10.33, -2.08) * mm, v(-10.68, -2.32) * mm, v(-10.94, -2.51) * mm, v(-11.18, -2.7) * mm, v(-11.41, -2.88) * mm, v(-11.62, -3.06) * mm, v(-11.88, -3.3) * mm, v(-12.17, -3.58) * mm, v(-12.46, -3.9) * mm, v(-12.67, -4.18) * mm, v(-12.82, -4.38) * mm, v(-12.97, -4.6) * mm, v(-13.08, -4.77) * mm, v(-13.16, -4.92) * mm, v(-13.2, -4.97) * mm, v(-13.23, -5.02) * mm, v(-13.26, -5.08) * mm, v(-13.3, -5.16) * mm, v(-13.35, -5.23) * mm, v(-13.4, -5.33) * mm, v(-13.44, -5.42) * mm, v(-13.48, -5.51) * mm, v(-13.5, -5.58) * mm, v(-13.54, -5.65) * mm, v(-13.56, -5.72) * mm, v(-13.57, -5.76) * mm, v(-13.58, -5.8) * mm, v(-13.6, -5.84) * mm, v(-13.6, -5.9) * mm, v(-13.62, -5.96) * mm, v(-13.63, -6.05) * mm, v(-13.65, -6.15) * mm, v(-13.66, -6.28) * mm, v(-13.68, -6.45) * mm, v(-13.68, -6.66) * mm, v(-13.68, -6.86) * mm, v(-13.67, -7.03) * mm, v(-13.66, -7.16) * mm, v(-13.65, -7.28) * mm, v(-13.64, -7.38) * mm, v(-13.62, -7.49) * mm, v(-13.6, -7.56) * mm, v(-13.58, -7.64) * mm, v(-13.56, -7.71) * mm, v(-13.53, -7.79) * mm, v(-13.5, -7.87) * mm, v(-13.47, -7.94) * mm, v(-13.4, -8.07) * mm, v(-13.34, -8.2) * mm, v(-13.27, -8.32) * mm, v(-13.2, -8.43) * mm, v(-13.14, -8.54) * mm, v(-13.04, -8.69) * mm, v(-12.95, -8.83) * mm, v(-12.84, -8.98) * mm, v(-12.76, -9.1) * mm, v(-12.68, -9.2) * mm, v(-12.6, -9.3) * mm, v(-12.52, -9.4) * mm, v(-12.44, -9.5) * mm, v(-12.37, -9.6) * mm, v(-12.3, -9.68) * mm, v(-12.22, -9.77) * mm, v(-12.15, -9.84) * mm, v(-12.09, -9.9) * mm, v(-12, -10) * mm, v(-11.92, -10.07) * mm, v(-11.84, -10.15) * mm, v(-11.77, -10.2) * mm, v(-11.7, -10.26) * mm, v(-11.61, -10.34) * mm, v(-11.49, -10.44) * mm, v(-11.25, -10.63) * mm, v(-10.94, -10.89) * mm, v(-10.54, -11.2) * mm, v(-10.24, -11.42) * mm, v(-10.06, -11.55) * mm, v(-9.93, -11.63) * mm, v(-9.79, -11.72) * mm, v(-9.62, -11.83) * mm, v(-9.44, -11.92) * mm, v(-9.3, -12) * mm, v(-9.18, -12.07) * mm, v(-9.05, -12.13) * mm, v(-8.88, -12.21) * mm, v(-8.6, -12.36) * mm, v(-8.24, -12.54) * mm, v(-7.77, -12.77) * mm, v(-7.36, -12.95) * mm, v(-7.05, -13.08) * mm, v(-6.88, -13.15) * mm, v(-6.61, -13.25) * mm, v(-6.02, -13.46) * mm, v(-5.05, -13.75) * mm, v(-4.05, -13.98) * mm, v(-3.26, -14.12) * mm, v(-2.77, -14.2) * mm, v(-2.4, -14.24) * mm, v(-2.02, -14.28) * mm, v(-1.57, -14.32) * mm, v(-1.05, -14.35) * mm, v(-0.53, -14.37) * mm, v(0, -14.36) * mm, v(0.57, -14.33) * mm, v(1.17, -14.29) * mm, v(1.79, -14.22) * mm, v(2.4, -14.14) * mm, v(3.17, -14) * mm, v(3.86, -13.84) * mm, v(4.5, -13.66) * mm, v(4.87, -13.54) * mm, v(5.16, -13.44) * mm, v(5.44, -13.34) * mm, v(5.8, -13.2) * mm, v(6.25, -13) * mm, v(6.76, -12.77) * mm, v(7.33, -12.48) * mm, v(7.83, -12.22) * mm, v(8.22, -12) * mm, v(8.62, -11.77) * mm, v(8.98, -11.55) * mm, v(9.32, -11.34) * mm, v(9.55, -11.18) * mm, v(9.76, -11.03) * mm, v(10.03, -10.84) * mm, v(10.28, -10.64) * mm, v(10.53, -10.43) * mm, v(10.72, -10.26) * mm, v(10.9, -10.08) * mm, v(11.18, -9.83) * mm, v(11.52, -9.5) * mm, v(11.93, -9.08) * mm, v(12.24, -8.74) * mm, v(12.47, -8.48) * mm, v(12.62, -8.3) * mm, v(12.76, -8.12) * mm, v(12.85, -8) * mm, v(12.92, -7.9) * mm, v(12.98, -7.8) * mm, v(13.03, -7.7) * mm, v(13.07, -7.63) * mm, v(13.1, -7.58) * mm, v(13.1, -7.55) * mm, v(13.12, -7.51) * mm, v(13.13, -7.47) * mm, v(13.15, -7.42) * mm, v(13.16, -7.37) * mm, v(13.17, -7.32) * mm, v(13.18, -7.24) * mm, v(13.2, -7.16) * mm, v(13.2, -7.07) * mm, v(13.21, -7) * mm, v(13.22, -6.92) * mm]});
            skArc(sketch, "E18.trimOffspring", {"start": v(9.85, -4.37) * mm, "mid": v(9.8, -3.34) * mm, "end": v(9.71, -2.3) * mm});
            skFitSpline(sketch, "E19.trimOffspring", {"points": [v(13.2, -7.07) * mm, v(13.21, -7) * mm, v(13.22, -6.92) * mm, v(13.22, -6.83) * mm, v(13.23, -6.71) * mm, v(13.23, -6.6) * mm, v(13.23, -6.53) * mm, v(13.22, -6.46) * mm, v(13.21, -6.41) * mm, v(13.2, -6.36) * mm, v(13.2, -6.3) * mm, v(13.16, -6.19) * mm, v(13.1, -6.02) * mm, v(13, -5.78) * mm, v(12.83, -5.45) * mm, v(12.57, -5.05) * mm, v(12.29, -4.66) * mm, v(11.97, -4.29) * mm, v(11.68, -3.98) * mm, v(11.43, -3.74) * mm, v(11.27, -3.59) * mm, v(11.14, -3.46) * mm, v(11, -3.35) * mm, v(10.77, -3.14) * mm, v(10.43, -2.84) * mm, v(9.97, -2.48) * mm, v(9.47, -2.13) * mm, v(8.91, -1.77) * mm, v(8.1, -1.29) * mm, v(7.24, -0.83) * mm, v(6.4, -0.43) * mm, v(5.61, -0.08) * mm, v(4.9, 0.18) * mm, v(4.18, 0.4) * mm, v(3.42, 0.58) * mm, v(2.54, 0.76) * mm, v(1.63, 0.9) * mm, v(1.07, 0.96) * mm, v(0.68, 1) * mm, v(0.47, 1) * mm, v(0.26, 1.02) * mm, v(0, 1.03) * mm, v(-0.3, 1.03) * mm, v(-0.6, 1.02) * mm, v(-0.97, 1) * mm, v(-1.43, 0.97) * mm, v(-1.98, 0.9) * mm, v(-2.52, 0.84) * mm, v(-3.04, 0.76) * mm, v(-3.48, 0.7) * mm, v(-3.83, 0.63) * mm, v(-4.18, 0.56) * mm, v(-4.63, 0.46) * mm, v(-5.18, 0.33) * mm, v(-5.73, 0.17) * mm, v(-6.27, 0) * mm, v(-6.78, -0.18) * mm, v(-7.26, -0.37) * mm, v(-7.74, -0.58) * mm, v(-8.14, -0.78) * mm, v(-8.48, -0.96) * mm, v(-8.74, -1.1) * mm, v(-9.01, -1.26) * mm, v(-9.38, -1.48) * mm, v(-9.86, -1.77) * mm, v(-10.33, -2.08) * mm, v(-10.68, -2.32) * mm, v(-10.94, -2.51) * mm, v(-11.18, -2.7) * mm, v(-11.41, -2.88) * mm, v(-11.62, -3.06) * mm, v(-11.88, -3.3) * mm, v(-12.17, -3.58) * mm, v(-12.46, -3.9) * mm, v(-12.67, -4.18) * mm, v(-12.82, -4.38) * mm, v(-12.97, -4.6) * mm, v(-13.08, -4.77) * mm, v(-13.16, -4.92) * mm, v(-13.2, -4.97) * mm, v(-13.23, -5.02) * mm, v(-13.26, -5.08) * mm, v(-13.3, -5.16) * mm, v(-13.35, -5.23) * mm, v(-13.4, -5.33) * mm, v(-13.44, -5.42) * mm, v(-13.48, -5.51) * mm, v(-13.5, -5.58) * mm, v(-13.54, -5.65) * mm, v(-13.56, -5.72) * mm, v(-13.57, -5.76) * mm, v(-13.58, -5.8) * mm, v(-13.6, -5.84) * mm, v(-13.6, -5.9) * mm, v(-13.62, -5.96) * mm, v(-13.63, -6.05) * mm, v(-13.65, -6.15) * mm, v(-13.66, -6.28) * mm, v(-13.68, -6.45) * mm, v(-13.68, -6.66) * mm, v(-13.68, -6.86) * mm, v(-13.67, -7.03) * mm, v(-13.66, -7.16) * mm, v(-13.65, -7.28) * mm, v(-13.64, -7.38) * mm, v(-13.62, -7.49) * mm, v(-13.6, -7.56) * mm, v(-13.58, -7.64) * mm, v(-13.56, -7.71) * mm, v(-13.53, -7.79) * mm, v(-13.5, -7.87) * mm, v(-13.47, -7.94) * mm, v(-13.4, -8.07) * mm, v(-13.34, -8.2) * mm, v(-13.27, -8.32) * mm, v(-13.2, -8.43) * mm, v(-13.14, -8.54) * mm, v(-13.04, -8.69) * mm, v(-12.95, -8.83) * mm, v(-12.84, -8.98) * mm, v(-12.76, -9.1) * mm, v(-12.68, -9.2) * mm, v(-12.6, -9.3) * mm, v(-12.52, -9.4) * mm, v(-12.44, -9.5) * mm, v(-12.37, -9.6) * mm, v(-12.3, -9.68) * mm, v(-12.22, -9.77) * mm, v(-12.15, -9.84) * mm, v(-12.09, -9.9) * mm, v(-12, -10) * mm, v(-11.92, -10.07) * mm, v(-11.84, -10.15) * mm, v(-11.77, -10.2) * mm, v(-11.7, -10.26) * mm, v(-11.61, -10.34) * mm, v(-11.49, -10.44) * mm, v(-11.25, -10.63) * mm, v(-10.94, -10.89) * mm, v(-10.54, -11.2) * mm, v(-10.24, -11.42) * mm, v(-10.06, -11.55) * mm, v(-9.93, -11.63) * mm, v(-9.79, -11.72) * mm, v(-9.62, -11.83) * mm, v(-9.44, -11.92) * mm, v(-9.3, -12) * mm, v(-9.18, -12.07) * mm, v(-9.05, -12.13) * mm, v(-8.88, -12.21) * mm, v(-8.6, -12.36) * mm, v(-8.24, -12.54) * mm, v(-7.77, -12.77) * mm, v(-7.36, -12.95) * mm, v(-7.05, -13.08) * mm, v(-6.88, -13.15) * mm, v(-6.61, -13.25) * mm, v(-6.02, -13.46) * mm, v(-5.05, -13.75) * mm, v(-4.05, -13.98) * mm, v(-3.26, -14.12) * mm, v(-2.77, -14.2) * mm, v(-2.4, -14.24) * mm, v(-2.02, -14.28) * mm, v(-1.57, -14.32) * mm, v(-1.05, -14.35) * mm, v(-0.53, -14.37) * mm, v(0, -14.36) * mm, v(0.57, -14.33) * mm, v(1.17, -14.29) * mm, v(1.79, -14.22) * mm, v(2.4, -14.14) * mm, v(3.17, -14) * mm, v(3.86, -13.84) * mm, v(4.5, -13.66) * mm, v(4.87, -13.54) * mm, v(5.16, -13.44) * mm, v(5.44, -13.34) * mm, v(5.8, -13.2) * mm, v(6.25, -13) * mm, v(6.76, -12.77) * mm, v(7.33, -12.48) * mm, v(7.83, -12.22) * mm, v(8.22, -12) * mm, v(8.62, -11.77) * mm, v(8.98, -11.55) * mm, v(9.32, -11.34) * mm, v(9.55, -11.18) * mm, v(9.76, -11.03) * mm, v(10.03, -10.84) * mm, v(10.28, -10.64) * mm, v(10.53, -10.43) * mm, v(10.72, -10.26) * mm, v(10.9, -10.08) * mm, v(11.18, -9.83) * mm, v(11.52, -9.5) * mm, v(11.93, -9.08) * mm, v(12.24, -8.74) * mm, v(12.47, -8.48) * mm, v(12.62, -8.3) * mm, v(12.76, -8.12) * mm, v(12.85, -8) * mm, v(12.92, -7.9) * mm, v(12.98, -7.8) * mm, v(13.03, -7.7) * mm, v(13.07, -7.63) * mm, v(13.1, -7.58) * mm, v(13.1, -7.55) * mm, v(13.12, -7.51) * mm, v(13.13, -7.47) * mm, v(13.15, -7.42) * mm, v(13.16, -7.37) * mm, v(13.17, -7.32) * mm, v(13.18, -7.24) * mm, v(13.2, -7.16) * mm, v(13.2, -7.07) * mm, v(13.21, -7) * mm, v(13.22, -6.92) * mm]});
            skArc(sketch, "E20.trimOffspring", {"start": v(7.29, -3.8) * mm, "mid": v(7.15, -2.25) * mm, "end": v(6.96, -0.7) * mm});
            skArc(sketch, "E21", {"start": v(-13.78, -4.7) * mm, "mid": v(-15.61, -6.48) * mm, "end": v(-13.94, -8.42) * mm});
            skArc(sketch, "E22", {"start": v(-14.2, -5.68) * mm, "mid": v(-15, -6.38) * mm, "end": v(-14.3, -7.18) * mm});
            skSolve(sketch);
        }
        {
            var Q0;
            Q0=makeQuery(id+"F0.imprint","IMPRINT",FACE,{"disambiguationData":[TD([[makeQuery(id+"F0.imprint","IMPRINT",EDGE,{"derivedFrom":sQuery(id+"F0.wireOp",EDGE,"E1")}),1.0]])]});
            extrude(context, id + "F2", {"entities" : qUnion([Q0]), "depth" : 3.8 * mm});
        }
        {
            var Q0;
            Q0=makeQuery(id+"F2.opExtrude","CAP_EDGE",EDGE,{"disambiguationData":[OSD([sQuery(id+"F0.wireOp",EDGE,"E1")])],"isStart":false});
            var Q1;
            Q1=makeQuery(id+"F2.opExtrude","CAP_EDGE",EDGE,{"disambiguationData":[OSD([sQuery(id+"F0.wireOp",EDGE,"E21")])],"isStart":false});
            var Q2;
            Q2=makeQuery(id+"F2.opExtrude","CAP_EDGE",EDGE,{"disambiguationData":[OSD([sQuery(id+"F0.wireOp",EDGE,"E1")])],"isStart":true});
            fillet(context, id + "F1", {"entities" : qUnion([Q0, Q1, Q2]), "radius" : 0.25 * mm, "tangentPropagation" : true, "allowEdgeOverflow" : false});
        }
    });
